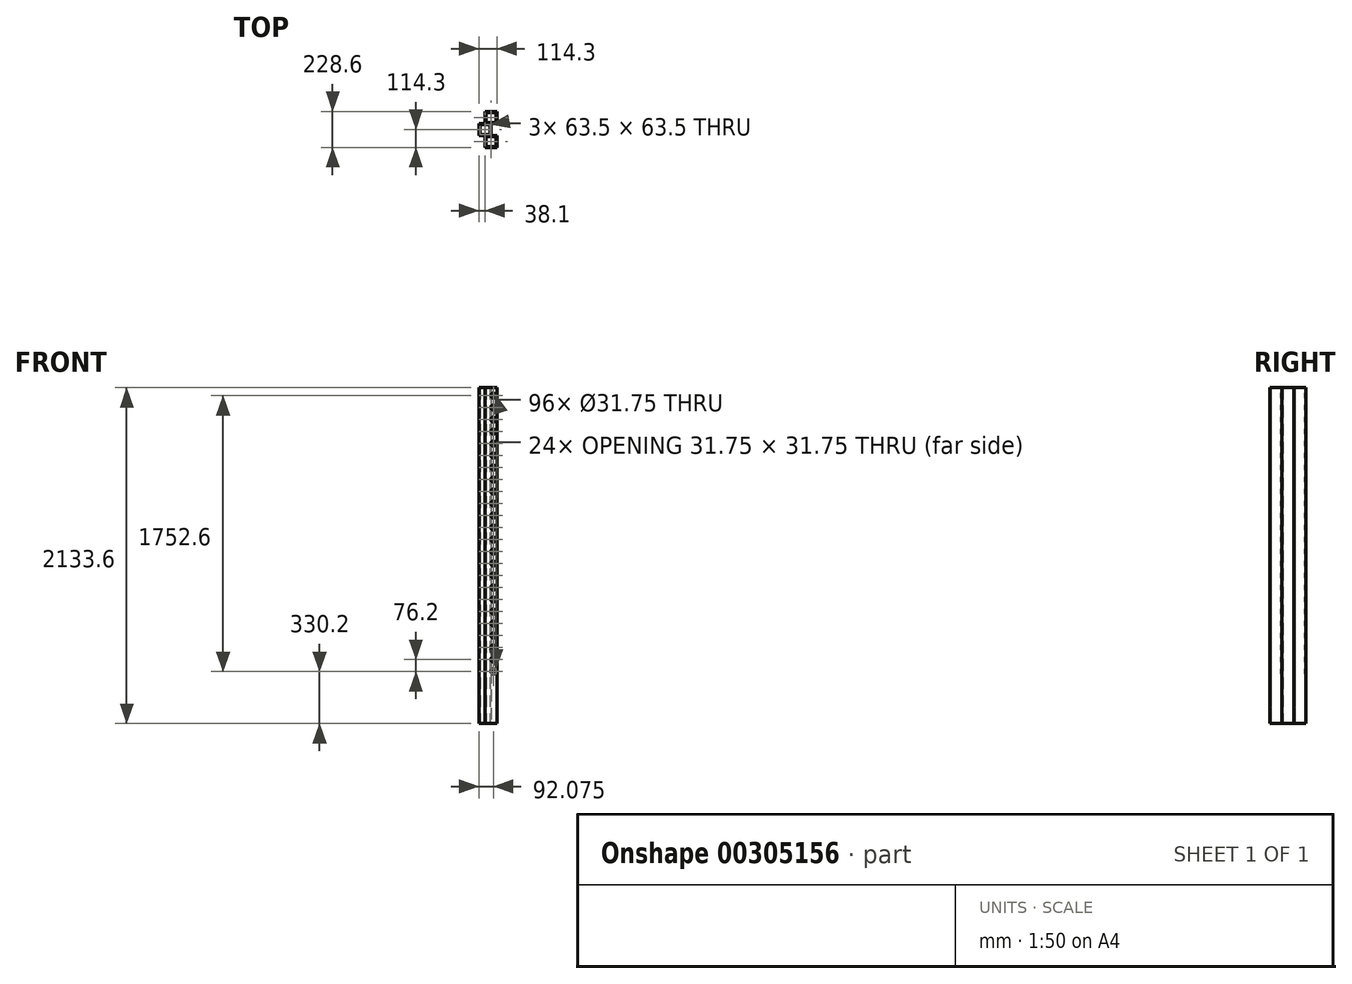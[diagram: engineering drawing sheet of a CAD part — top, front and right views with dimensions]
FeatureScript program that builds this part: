
annotation { "Feature Type Name" : "Feature", "Feature Type Description" : "" }
export const myFeature = defineFeature(function(context is Context, id is Id, definition is map)
    precondition{}
    {
        {
            var Q0;
            Q0=qCreatedBy(makeId("Top.planeOp"),FACE);
            var sketch = newSketch(context, id + "F0", { "sketchPlane" : qUnion([Q0])});
            skLineSegment(sketch, "E0.bottom", {"start": v(-609.6, 38.1) * mm, "end": v(-685.8, 38.1) * mm});
            skLineSegment(sketch, "E0.top", {"start": v(-609.6, -38.1) * mm, "end": v(-685.8, -38.1) * mm});
            skLineSegment(sketch, "E0.left", {"start": v(-609.6, 38.1) * mm, "end": v(-609.6, -38.1) * mm});
            skLineSegment(sketch, "E0.right", {"start": v(-685.8, 38.1) * mm, "end": v(-685.8, -38.1) * mm});
            skPoint(sketch, "E0.middle", {"position": v(-647.7, 0) * mm});
            skLineSegment(sketch, "E1", {"start": v(-647.7, -38.1) * mm, "end": v(-647.7, -114.3) * mm});
            skLineSegment(sketch, "E2", {"start": v(-647.7, -114.3) * mm, "end": v(-571.5, -114.3) * mm});
            skLineSegment(sketch, "E3", {"start": v(-571.5, -114.3) * mm, "end": v(-571.5, -38.1) * mm});
            skLineSegment(sketch, "E4", {"start": v(-571.5, -38.1) * mm, "end": v(-609.6, -38.1) * mm});
            skLineSegment(sketch, "E5", {"start": v(-647.7, 38.1) * mm, "end": v(-647.7, 114.3) * mm});
            skLineSegment(sketch, "E6", {"start": v(-647.7, 114.3) * mm, "end": v(-571.5, 114.3) * mm});
            skLineSegment(sketch, "E7", {"start": v(-571.5, 114.3) * mm, "end": v(-571.5, 38.1) * mm});
            skLineSegment(sketch, "E8", {"start": v(-571.5, 38.1) * mm, "end": v(-609.6, 38.1) * mm});
            skLineSegment(sketch, "E9.0", {"start": v(-615.95, 31.75) * mm, "end": v(-679.45, 31.75) * mm});
            skLineSegment(sketch, "E9.1", {"start": v(-615.95, 31.75) * mm, "end": v(-615.95, -31.75) * mm});
            skLineSegment(sketch, "E9.2", {"start": v(-615.95, -31.75) * mm, "end": v(-679.45, -31.75) * mm});
            skLineSegment(sketch, "E9.3", {"start": v(-679.45, 31.75) * mm, "end": v(-679.45, -31.75) * mm});
            skLineSegment(sketch, "E10.bottom", {"start": v(-641.35, 107.95) * mm, "end": v(-577.85, 107.95) * mm});
            skLineSegment(sketch, "E10.top", {"start": v(-641.35, 44.45) * mm, "end": v(-577.85, 44.45) * mm});
            skLineSegment(sketch, "E10.left", {"start": v(-641.35, 107.95) * mm, "end": v(-641.35, 44.45) * mm});
            skLineSegment(sketch, "E10.right", {"start": v(-577.85, 107.95) * mm, "end": v(-577.85, 44.45) * mm});
            skPoint(sketch, "E10.middle", {"position": v(-609.6, 76.2) * mm});
            skPoint(sketch, "E10.middle.positionSnap0", {"position": v(-571.5, 76.2) * mm});
            skPoint(sketch, "E10.middle.positionSnap1", {"position": v(-609.6, 114.3) * mm});
            skPoint(sketch, "E10.centerSnap0", {"position": v(-571.5, 76.2) * mm});
            skPoint(sketch, "E10.centerSnap1", {"position": v(-609.6, 114.3) * mm});
            skLineSegment(sketch, "E11.bottom", {"start": v(-641.35, -44.45) * mm, "end": v(-577.85, -44.45) * mm});
            skLineSegment(sketch, "E11.top", {"start": v(-641.35, -107.95) * mm, "end": v(-577.85, -107.95) * mm});
            skLineSegment(sketch, "E11.left", {"start": v(-641.35, -44.45) * mm, "end": v(-641.35, -107.95) * mm});
            skLineSegment(sketch, "E11.right", {"start": v(-577.85, -44.45) * mm, "end": v(-577.85, -107.95) * mm});
            skPoint(sketch, "E11.middle", {"position": v(-609.6, -76.2) * mm});
            skPoint(sketch, "E11.middle.positionSnap0", {"position": v(-609.6, -114.3) * mm});
            skPoint(sketch, "E11.middle.positionSnap1", {"position": v(-647.7, -76.2) * mm});
            skPoint(sketch, "E11.centerSnap0", {"position": v(-609.6, -114.3) * mm});
            skPoint(sketch, "E11.centerSnap1", {"position": v(-647.7, -76.2) * mm});
            skSolve(sketch);
        }
        {
            var Q0;
            {var subQ2=sQuery(id+"F0.wireOp",EDGE,"E5");Q0=makeQuery(id+"F0.imprint","IMPRINT",FACE,{"disambiguationData":[TD([[makeQuery(id+"F0.imprint","IMPRINT",EDGE,{"derivedFrom":subQ2}),-1.0]])]});}
            var Q1;
            {var subQ3=sQuery(id+"F0.wireOp",EDGE,"E0.left");Q1=makeQuery(id+"F0.imprint","IMPRINT",FACE,{"disambiguationData":[TD([[makeQuery(id+"F0.imprint","IMPRINT",EDGE,{"derivedFrom":subQ3}),-1.0]])]});}
            var Q2;
            {var subQ0=sQuery(id+"F0.wireOp",EDGE,"E1");Q2=makeQuery(id+"F0.imprint","IMPRINT",FACE,{"disambiguationData":[TD([[makeQuery(id+"F0.imprint","IMPRINT",EDGE,{"derivedFrom":subQ0}),1.0]])]});}
            extrude(context, id + "F1", {"entities" : qUnion([Q0, Q1, Q2]), "depth" : 2133.6 * mm});
        }
        {
            var Q0;
            Q0=makeQuery(id+"F1.opExtrude","SWEPT_FACE",FACE,{"disambiguationData":[OSD([sQuery(id+"F0.wireOp",EDGE,"E2")])]});
            var sketch = newSketch(context, id + "F2", { "sketchPlane" : qUnion([Q0])});
            skCircle(sketch, "E12", {"center": v(-593.73, 2082.8) * mm, "radius": 15.88 * mm});
            skCircle(sketch, "E13.0.1.0", {"center": v(-593.73, 2006.6) * mm, "radius": 15.88 * mm});
            skCircle(sketch, "E13.0.2.0", {"center": v(-593.73, 1930.4) * mm, "radius": 15.88 * mm});
            skCircle(sketch, "E13.0.3.0", {"center": v(-593.73, 1854.2) * mm, "radius": 15.88 * mm});
            skCircle(sketch, "E13.0.4.0", {"center": v(-593.73, 1778) * mm, "radius": 15.88 * mm});
            skCircle(sketch, "E13.0.5.0", {"center": v(-593.73, 1701.8) * mm, "radius": 15.88 * mm});
            skCircle(sketch, "E13.0.6.0", {"center": v(-593.72, 1625.6) * mm, "radius": 15.88 * mm});
            skCircle(sketch, "E13.0.7.0", {"center": v(-593.72, 1549.4) * mm, "radius": 15.88 * mm});
            skCircle(sketch, "E13.0.8.0", {"center": v(-593.72, 1473.2) * mm, "radius": 15.88 * mm});
            skCircle(sketch, "E13.0.9.0", {"center": v(-593.72, 1397) * mm, "radius": 15.88 * mm});
            skCircle(sketch, "E13.0.10.0", {"center": v(-593.72, 1320.8) * mm, "radius": 15.88 * mm});
            skCircle(sketch, "E13.0.11.0", {"center": v(-593.72, 1244.6) * mm, "radius": 15.88 * mm});
            skCircle(sketch, "E13.0.12.0", {"center": v(-593.72, 1168.4) * mm, "radius": 15.88 * mm});
            skCircle(sketch, "E13.0.13.0", {"center": v(-593.72, 1092.2) * mm, "radius": 15.88 * mm});
            skCircle(sketch, "E13.0.14.0", {"center": v(-593.72, 1016) * mm, "radius": 15.88 * mm});
            skCircle(sketch, "E13.0.15.0", {"center": v(-593.72, 939.8) * mm, "radius": 15.88 * mm});
            skCircle(sketch, "E13.0.16.0", {"center": v(-593.72, 863.6) * mm, "radius": 15.88 * mm});
            skCircle(sketch, "E13.0.17.0", {"center": v(-593.72, 787.4) * mm, "radius": 15.88 * mm});
            skCircle(sketch, "E13.0.18.0", {"center": v(-593.72, 711.2) * mm, "radius": 15.88 * mm});
            skCircle(sketch, "E13.0.19.0", {"center": v(-593.72, 635) * mm, "radius": 15.88 * mm});
            skCircle(sketch, "E13.0.20.0", {"center": v(-593.72, 558.8) * mm, "radius": 15.88 * mm});
            skCircle(sketch, "E13.0.21.0", {"center": v(-593.72, 482.6) * mm, "radius": 15.88 * mm});
            skCircle(sketch, "E13.0.22.0", {"center": v(-593.72, 406.4) * mm, "radius": 15.88 * mm});
            skCircle(sketch, "E13.0.23.0", {"center": v(-593.72, 330.2) * mm, "radius": 15.88 * mm});
            skLineSegment(sketch, "E13.direction1", {"start": v(-593.73, 2082.8) * mm, "end": v(-569.91, 2082.8) * mm, "construction": true});
            skLineSegment(sketch, "E13.direction2", {"start": v(-593.73, 2082.8) * mm, "end": v(-593.73, 2006.6) * mm, "construction": true});
            skSolve(sketch);
        }
        {
            var Q0;
            Q0 = qSketchRegion(id + "F2", true);
            var Q1;
            Q1=makeQuery(id+"F1.opExtrude","SWEPT_FACE",FACE,{"disambiguationData":[OSD([sQuery(id+"F0.wireOp",EDGE,"E6")])]});
            extrude(context, id + "F3", {"entities" : qUnion([Q0]), "operationType" : NewBodyOperationType.REMOVE, "endBound" : BoundingType.UP_TO_SURFACE, "oppositeDirection" : true, "endBoundEntityFace" : qUnion([Q1]), "depth" : 25.4 * mm});
        }
    });
